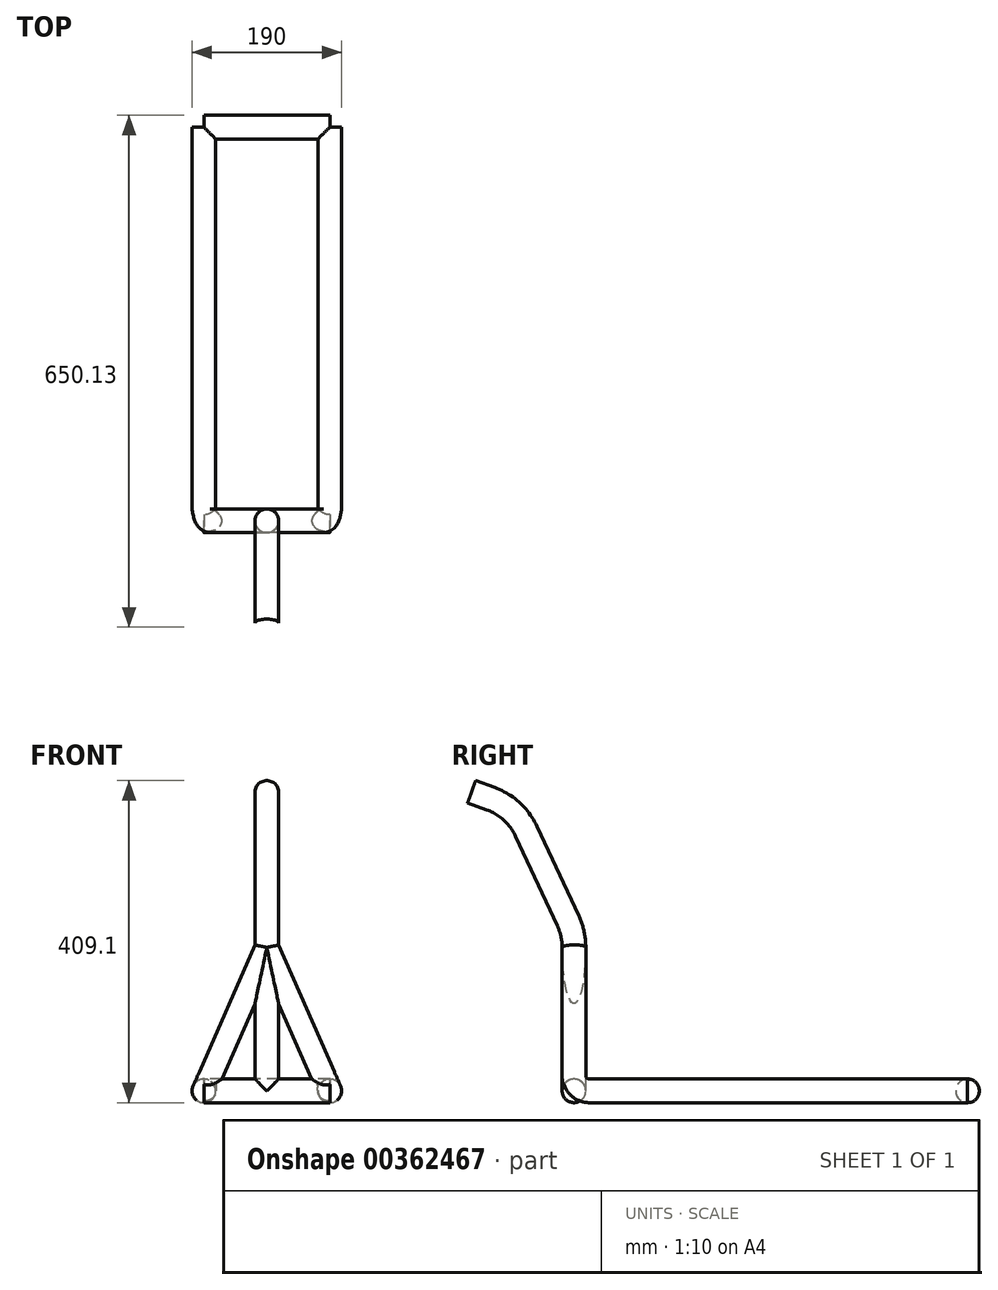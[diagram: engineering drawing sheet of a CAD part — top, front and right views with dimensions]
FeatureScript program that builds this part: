
annotation { "Feature Type Name" : "Feature", "Feature Type Description" : "" }
export const myFeature = defineFeature(function(context is Context, id is Id, definition is map)
    precondition{}
    {
        {
            var Q0;
            Q0=qCreatedBy(makeId("Right.planeOp"),FACE);
            var sketch = newSketch(context, id + "F0", { "sketchPlane" : qUnion([Q0])});
            skLineSegment(sketch, "E0", {"start": v(0, 0) * mm, "end": v(500, 0) * mm});
            skLineSegment(sketch, "E1", {"start": v(500, 0) * mm, "end": v(500, 400) * mm});
            skLineSegment(sketch, "E2", {"start": v(500, 400) * mm, "end": v(900, 400) * mm});
            skLineSegment(sketch, "E3", {"start": v(0, 0) * mm, "end": v(0, 182.26) * mm});
            skLineSegment(sketch, "E4", {"start": v(-7.5, 216.07) * mm, "end": v(-60.51, 329.77) * mm});
            skLineSegment(sketch, "E5", {"start": v(-105.66, 371.14) * mm, "end": v(-130, 380) * mm});
            skPoint(sketch, "E6.visualSharp", {"position": v(-74.52, 359.8) * mm});
            skArc(sketch, "E6.filletArc", {"start": v(-60.51, 329.77) * mm, "mid": v(-78.97, 354.95) * mm, "end": v(-105.66, 371.14) * mm});
            skPoint(sketch, "E7.visualSharp", {"position": v(0, 200) * mm});
            skArc(sketch, "E7.filletArc", {"start": v(0, 182.26) * mm, "mid": v(-1.9, 199.58) * mm, "end": v(-7.5, 216.07) * mm});
            skSolve(sketch);
        }
        {
            var Q0;
            Q0=qCreatedBy(makeId("Front.planeOp"),FACE);
            var sketch = newSketch(context, id + "F1", { "sketchPlane" : qUnion([Q0])});
            skLineSegment(sketch, "E8", {"start": v(80, 0) * mm, "end": v(-80, 0) * mm});
            skSolve(sketch);
        }
        {
            var Q0;
            Q0=sQuery(id+"F0.wireOp",VERTEX,"E0.end");
            var Q1;
            Q1=sQuery(id+"F0.wireOp",EDGE,"E0");
            cPlane(context, id + "F2", {"entities" : qUnion([Q0, Q1]), "cplaneType" : CPlaneType.LINE_POINT, "offset" : 25 * mm, "width" : 150 * mm, "height" : 150 * mm});
        }
        {
            var Q0;
            Q0=qCreatedBy(id+"F2.planeOp",FACE);
            var sketch = newSketch(context, id + "F3", { "sketchPlane" : qUnion([Q0])});
            skLineSegment(sketch, "E9.0", {"start": v(-80, 0) * mm, "end": v(80, 0) * mm});
            skSolve(sketch);
        }
        {
            var Q0;
            Q0=sQuery(id+"F1.wireOp",VERTEX,"E8.start");
            var Q1;
            Q1=sQuery(id+"F3.wireOp",VERTEX,"E9.0.start");
            var Q2;
            Q2=sQuery(id+"F0.wireOp",VERTEX,"E3.end");
            cPlane(context, id + "F4", {"entities" : qUnion([Q0, Q1, Q2]), "cplaneType" : CPlaneType.THREE_POINT, "offset" : 25 * mm, "width" : 150 * mm, "height" : 150 * mm});
        }
        {
            var Q0;
            Q0=qCreatedBy(id+"F4.planeOp",FACE);
            var sketch = newSketch(context, id + "F5", { "sketchPlane" : qUnion([Q0])});
            skPoint(sketch, "E10.0", {"position": v(0, 166.9) * mm});
            skPoint(sketch, "E11.0", {"position": v(0, -32.15) * mm});
            skPoint(sketch, "E12.0", {"position": v(-500, -32.15) * mm});
            skLineSegment(sketch, "E13", {"start": v(0, 166.9) * mm, "end": v(0, -12.15) * mm});
            skLineSegment(sketch, "E14", {"start": v(-500, -32.15) * mm, "end": v(-20, -32.15) * mm});
            skArc(sketch, "E15.filletArc", {"start": v(-20, -32.15) * mm, "mid": v(-5.86, -26.3) * mm, "end": v(0, -12.15) * mm});
            skSolve(sketch);
        }
        {
            var Q0;
            Q0=qCreatedBy(id+"F2.planeOp",FACE);
            var sketch = newSketch(context, id + "F6", { "sketchPlane" : qUnion([Q0])});
            skPoint(sketch, "E16.0", {"position": v(-80, 0) * mm});
            skCircle(sketch, "E17", {"center": v(-80, 0) * mm, "radius": 15 * mm});
            skSolve(sketch);
        }
        {
            var Q0;
            Q0=makeQuery(id+"F6.imprint","IMPRINT",FACE,{"disambiguationData":[TD([[makeQuery(id+"F6.imprint","IMPRINT",EDGE,{"derivedFrom":sQuery(id+"F6.wireOp",EDGE,"E17")}),1.0]])]});
            var Q1;
            Q1=sQuery(id+"F5.wireOp",EDGE,"E14");
            var Q2;
            Q2=sQuery(id+"F5.wireOp",EDGE,"E15.filletArc");
            var Q3;
            Q3=sQuery(id+"F5.wireOp",EDGE,"E13");
            sweep(context, id + "F7", {"profiles" : qUnion([Q0]), "path" : qUnion([Q1, Q2, Q3])});
        }
        {
            var Q0;
            Q0=makeQuery(id+"F7.opSweep","SWEPT_BODY",BODY,{"disambiguationData":[OSD([sQuery(id+"F5.wireOp",EDGE,"E13"),sQuery(id+"F6.wireOp",EDGE,"E17")])]});
            var Q1;
            Q1=qCreatedBy(makeId("Right.planeOp"),FACE);
            mirror(context, id + "F8", {"operationType" : NewBodyOperationType.ADD, "entities" : qUnion([Q0]), "mirrorPlane" : qUnion([Q1])});
        }
        {
            var Q0;
            Q0=qCreatedBy(makeId("Top.planeOp"),FACE);
            var sketch = newSketch(context, id + "F9", { "sketchPlane" : qUnion([Q0])});
            skCircle(sketch, "E18", {"center": v(0, 0) * mm, "radius": 15 * mm});
            skSolve(sketch);
        }
        {
            var Q0;
            Q0=makeQuery(id+"F9.imprint","IMPRINT",FACE,{"disambiguationData":[TD([[makeQuery(id+"F9.imprint","IMPRINT",EDGE,{"derivedFrom":sQuery(id+"F9.wireOp",EDGE,"E18")}),1.0]])]});
            var Q1;
            Q1=sQuery(id+"F0.wireOp",EDGE,"E3");
            var Q2;
            Q2=sQuery(id+"F0.wireOp",EDGE,"E7.filletArc");
            var Q3;
            Q3=sQuery(id+"F0.wireOp",EDGE,"E4");
            var Q4;
            Q4=sQuery(id+"F0.wireOp",EDGE,"E6.filletArc");
            var Q5;
            Q5=sQuery(id+"F0.wireOp",EDGE,"E5");
            sweep(context, id + "F10", {"operationType" : NewBodyOperationType.ADD, "profiles" : qUnion([Q0]), "path" : qUnion([Q1, Q2, Q3, Q4, Q5])});
        }
        {
            var Q0;
            Q0=qCreatedBy(makeId("Right.planeOp"),FACE);
            var sketch = newSketch(context, id + "F11", { "sketchPlane" : qUnion([Q0])});
            skCircle(sketch, "E19", {"center": v(0, 0) * mm, "radius": 15 * mm});
            skPoint(sketch, "E20.0", {"position": v(500, 0) * mm});
            skCircle(sketch, "E21", {"center": v(500, 0) * mm, "radius": 15 * mm});
            skSolve(sketch);
        }
        {
            var Q0;
            Q0=makeQuery(id+"F11.imprint","IMPRINT",FACE,{"disambiguationData":[TD([[makeQuery(id+"F11.imprint","IMPRINT",EDGE,{"derivedFrom":sQuery(id+"F11.wireOp",EDGE,"E19")}),1.0]])]});
            var Q1;
            Q1=makeQuery(id+"F11.imprint","IMPRINT",FACE,{"disambiguationData":[TD([[makeQuery(id+"F11.imprint","IMPRINT",EDGE,{"derivedFrom":sQuery(id+"F11.wireOp",EDGE,"E21")}),1.0]])]});
            extrude(context, id + "F12", {"entities" : qUnion([Q0, Q1]), "operationType" : NewBodyOperationType.ADD, "depth" : 80 * mm, "offsetDistance" : 25 * mm, "hasSecondDirection" : true, "secondDirectionOppositeDirection" : true, "secondDirectionDepth" : 80 * mm});
        }
    });
